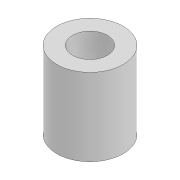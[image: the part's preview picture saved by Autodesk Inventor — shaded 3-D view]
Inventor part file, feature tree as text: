
AUTODESK INVENTOR PART (.ipt)
format: ipt  version: 2020 (Build 240168000, 168)  size: 81,408 bytes
history: native  units: mm
features: extrude x1, sketch x1
ambient origin geometry x8: Origin, YZ Plane, XZ Plane, XY Plane, X Axis, Y Axis, Z Axis, Center Point
bodies: Solid1 (feature_tree)
feature tree (2):
  extrude  "Extrusion1"  Depth=14.0mm
  sketch  "Sketch1"  dims[d0=6.3mm d2=12.0mm d3=14.0mm d4=0.0mm]
